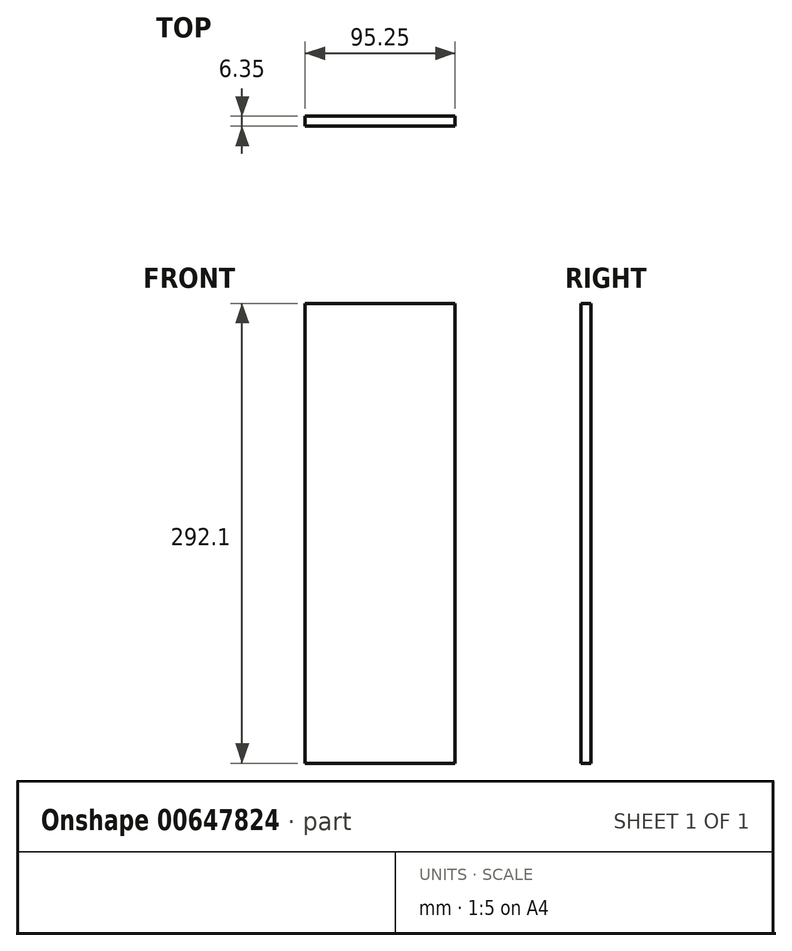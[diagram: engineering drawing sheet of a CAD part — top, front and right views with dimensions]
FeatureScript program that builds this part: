
annotation { "Feature Type Name" : "Feature", "Feature Type Description" : "" }
export const myFeature = defineFeature(function(context is Context, id is Id, definition is map)
    precondition{}
    {
        {
            var Q0;
            Q0=qCreatedBy(makeId("Front.planeOp"),FACE);
            var sketch = newSketch(context, id + "F0", { "sketchPlane" : qUnion([Q0])});
            skLineSegment(sketch, "E0.bottom", {"start": v(-89.02, -75.44) * mm, "end": v(6.23, -75.44) * mm});
            skLineSegment(sketch, "E0.top", {"start": v(-89.02, 216.66) * mm, "end": v(6.23, 216.66) * mm});
            skLineSegment(sketch, "E0.left", {"start": v(-89.02, -75.44) * mm, "end": v(-89.02, 216.66) * mm});
            skLineSegment(sketch, "E0.right", {"start": v(6.23, -75.44) * mm, "end": v(6.23, 216.66) * mm});
            skSolve(sketch);
        }
        {
            var Q0;
            Q0=makeQuery(id+"F0.imprint","IMPRINT",FACE,{"disambiguationData":[TD([[makeQuery(id+"F0.imprint","IMPRINT",EDGE,{"derivedFrom":sQuery(id+"F0.wireOp",EDGE,"E0.bottom")}),1.0]])]});
            extrude(context, id + "F1", {"entities" : qUnion([Q0]), "depth" : 6.35 * mm, "offsetDistance" : 25.4 * mm});
        }
    });
